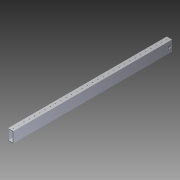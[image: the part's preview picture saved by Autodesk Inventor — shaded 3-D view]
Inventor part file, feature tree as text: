
AUTODESK INVENTOR PART (.ipt)
format: ipt  version: 2014 (Build 180170000, 170)  size: 759,296 bytes
history: native  units: in
note: dims shown in document units (in); Inventor stores cm internally (conversion verified against a paired STEP export)
features: other x2, extrude x2, sketch x2, imported_body x1
ambient origin geometry x8: Origin, YZ Plane, XZ Plane, XY Plane, X Axis, Y Axis, Z Axis, Center Point
bodies: Body1 (feature_tree)
feature tree (7):
  other  "Cut-Extrude2"
  other  "2x1 Tube1"
  extrude  "Extrusion1"  Depth=0.5in
  extrude  "Extrusion2"  Depth=1.0in TaperAngle=0.0deg
  imported_body  "Base1"
  sketch  "Sketch1"  dims[d0=29.0in d1=0.0in d2=0.5in]
  sketch  "Sketch2"  dims[d3=0.5in d4=1.0in d5=0.0in]
